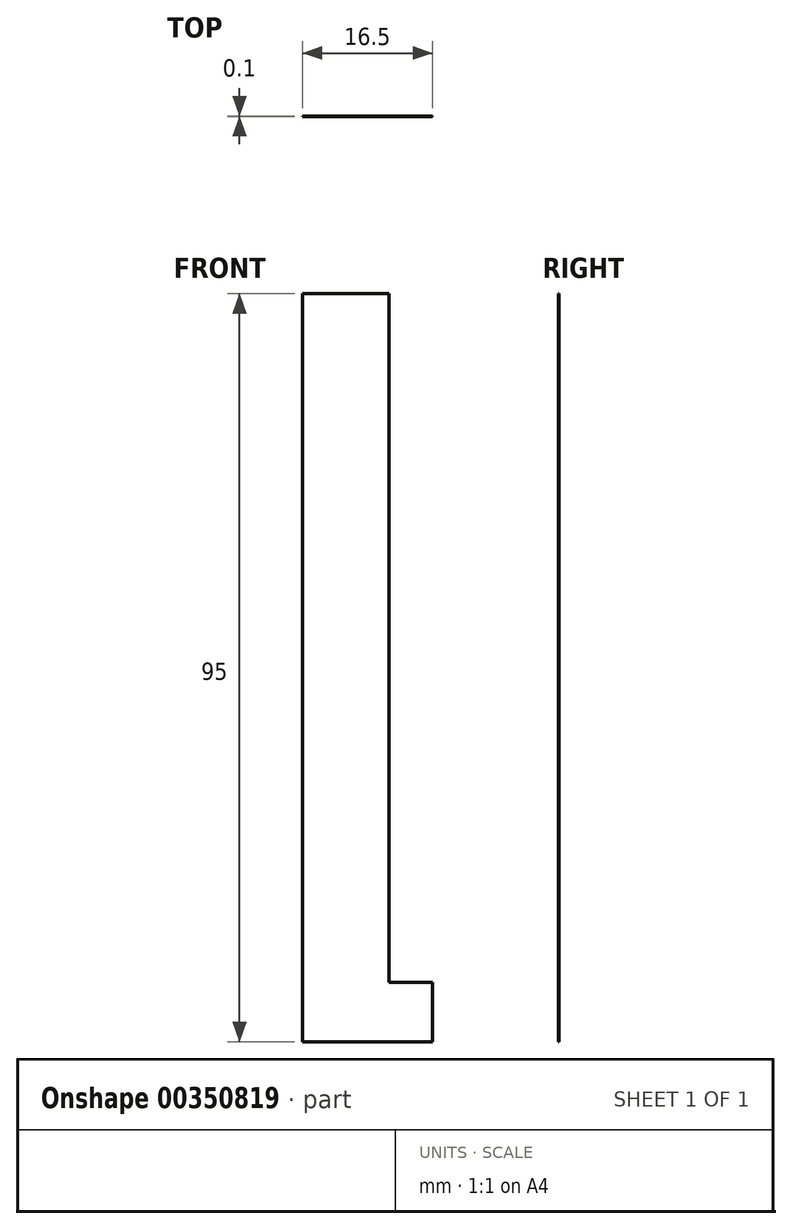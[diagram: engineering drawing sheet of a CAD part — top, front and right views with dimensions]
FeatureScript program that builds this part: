
annotation { "Feature Type Name" : "Feature", "Feature Type Description" : "" }
export const myFeature = defineFeature(function(context is Context, id is Id, definition is map)
    precondition{}
    {
        {
            var Q0;
            Q0=qCreatedBy(makeId("Front.planeOp"),FACE);
            var sketch = newSketch(context, id + "F0", { "sketchPlane" : qUnion([Q0])});
            skLineSegment(sketch, "E0.bottom", {"start": v(-8, 0) * mm, "end": v(3, 0) * mm});
            skLineSegment(sketch, "E0.top", {"start": v(-8, 95) * mm, "end": v(3, 95) * mm});
            skLineSegment(sketch, "E0.left", {"start": v(-8, 0) * mm, "end": v(-8, 95) * mm});
            skLineSegment(sketch, "E0.right", {"start": v(3, 7.5) * mm, "end": v(3, 95) * mm});
            skLineSegment(sketch, "E1", {"start": v(3, 0) * mm, "end": v(8.5, 0) * mm});
            skLineSegment(sketch, "E2", {"start": v(8.5, 0) * mm, "end": v(8.5, 7.5) * mm});
            skLineSegment(sketch, "E3", {"start": v(8.5, 7.5) * mm, "end": v(3, 7.5) * mm});
            skSolve(sketch);
        }
        {
            var Q0;
            Q0 = qSketchRegion(id + "F0", true);
            extrude(context, id + "F1", {"entities" : qUnion([Q0]), "depth" : 0.1 * mm});
        }
    });
